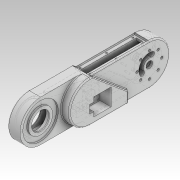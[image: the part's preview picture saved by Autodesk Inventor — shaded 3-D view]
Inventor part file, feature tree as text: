
AUTODESK INVENTOR PART (.ipt)
format: ipt  version: 2020 (Build 240168000, 168)  size: 708,096 bytes
history: native  units: mm
features: sketch x28, extrude x26, fillet x3, plane x2, revolve x2, projected_geometry x1
ambient origin geometry x8: Origin, YZ Plane, XZ Plane, XY Plane, X Axis, Y Axis, Z Axis, Center Point
bodies: Solid1 (feature_tree)
feature tree (62):
  extrude  "Extrusion1"  Depth=250.0mm
  extrude  "Extrusion3"  Depth=50.0mm TaperAngle=0.0deg
  extrude  "Extrusion6"  TaperAngle=0.0deg  [1 undecoded]
  extrude  "Extrusion7"  Depth=50.0mm
  extrude  "Extrusion8"  Depth=10.0mm TaperAngle=0.0deg
  extrude  "Extrusion9"  TaperAngle=0.0deg  [1 undecoded]
  extrude  "Extrusion10"  TaperAngle=30.0deg  [1 undecoded]
  extrude  "Extrusion11"  Depth=16.15mm
  extrude  "Extrusion12"  Depth=60.0mm
  plane  "Work Plane1"
  extrude  "Extrusion13"  Depth=10.0mm TaperAngle=0.0deg
  revolve  "Revolution1"  [1 undecoded]
  extrude  "Extrusion14"  Depth=86.0mm
  extrude  "Extrusion15"  Depth=4.0mm TaperAngle=0.0deg
  extrude  "Extrusion16"  Depth=70.0mm
  revolve  "Revolution2"  [1 undecoded]
  extrude  "Extrusion17"  Depth=7.3mm
  fillet  "Fillet1"  [1 undecoded]
  plane  "Work Plane2"
  extrude  "Extrusion18"  Depth=34.0mm
  extrude  "Extrusion19"  Depth=3.0mm TaperAngle=0.0deg
  extrude  "Extrusion20"  Depth=15.0mm TaperAngle=0.0deg
  extrude  "Extrusion21"  Depth=130.0mm
  extrude  "Extrusion25"  Depth=6.0mm TaperAngle=360.0deg
  extrude  "Extrusion22"  Depth=1.0mm
  fillet  "Fillet2"  Radius=5.2mm
  fillet  "Fillet3"  Radius=1.0mm
  extrude  "Extrusion23"  TaperAngle=90.0deg  [1 undecoded]
  extrude  "Extrusion24"  Depth=20.0mm
  extrude  "Extrusion26"  Depth=19.198622mm
  extrude  "Extrusion27"  Depth=50.0mm
  extrude  "Extrusion28"  TaperAngle=0.0deg  [1 undecoded]
  extrude  "CHOP"  Depth=12.0mm
  sketch  "Sketch1"  dims[d0=50.0mm d1=250.0mm]
  sketch  "Sketch3"  dims[d2=47.2mm d3=50.0mm d4=0.0mm]
  sketch  "Sketch6"  dims[d10=5.0mm d11=0.0mm d12=0.0mm]
  sketch  "Sketch7"  dims[d19=50.0mm d20=0.0mm d21=8.726646mm]
  projected_geometry  "Projected Loop1"
  sketch  "Sketch8"  dims[d22=75.0mm d25=10.0mm d26=0.0mm]
  sketch  "Sketch9"  dims[d27=50.0mm d30=0.0mm d31=0.0mm]
  sketch  "Sketch10"  dims[d33=30.0deg d34=30.0deg]
  sketch  "Sketch11"  dims[d35=0.0mm d36=0.0mm d37=16.15mm]
  sketch  "Sketch12"  dims[d38=3.3mm d39=60.0mm]
  sketch  "Sketch13"  dims[d40=80.0mm d42=360.0deg d44=10.0mm d45=0.0mm]
  sketch  "Sketch14"  dims[d50=42.0mm d51=42.0mm d52=0.0mm d53=0.0mm]
  sketch  "Sketch15"  dims[d54=38.0mm d55=86.0mm]
  sketch  "Sketch16"  dims[d56=59.0mm d57=4.0mm d58=0.0mm]
  sketch  "Sketch17"  dims[d59=-2.0mm d60=70.0mm]
  sketch  "Sketch18"  dims[d61=40.0mm d62=18.0mm d63=0.0mm]
  sketch  "Sketch19"  dims[d64=1.5mm d65=7.3mm d66=90.0deg]
  sketch  "Sketch20"  dims[d67=22.0mm d68=34.0mm]
  sketch  "Sketch21"  dims[d69=3.5mm d70=3.0mm d71=0.0mm]
  sketch  "Sketch22"  dims[d72=0.0mm d73=15.0mm d74=0.0mm]
  sketch  "Sketch23"  dims[d75=15.0mm d76=130.0mm]
  sketch  "Sketch24"  dims[d77=6.0mm d78=80.0mm d80=360.0deg]
  sketch  "Sketch25"  dims[d82=15.0mm d83=0.0mm d84=5.2mm d85=5.2mm d86=1.0mm]
  sketch  "Sketch26"  dims[d87=1.5mm d88=90.0deg]
  sketch  "Sketch27"  dims[d89=5.5mm d90=20.0mm]
  sketch  "Sketch28"  dims[d91=30.0deg d92=19.198622mm]
  sketch  "Sketch29"  dims[d93=15.0mm d94=0.0mm d95=50.0mm]
  sketch  "Sketch30"  dims[d96=30.0mm d97=0.0mm]
  sketch  "Sketch31"  dims[d98=8.0mm d99=12.0mm d100=6.1mm d101=13.0mm d102=125.0mm d103=75.0mm d104=0.0mm d105=0.0mm d106=2.1mm d107=10.0mm d108=10.0mm d109=32.0mm d110=110.0mm d111=0.0mm d112=3.0mm d113=3.0mm d114=5.0mm d115=1.0mm d116=4.0mm d117=0.0mm d118=4.0mm d119=4.0mm d120=32.25mm d121=0.0mm d122=3.0mm d124=0.5mm d125=0.0mm d126=3.0mm d127=2.0mm d128=8.0mm d129=8.0mm d130=4.0mm d131=4.0mm d132=3.9mm d133=6.0mm d134=0.0mm d135=4.0mm d136=0.0mm d137=60.0mm d138=0.5mm d139=0.0mm d140=3.0mm d141=10.0mm d142=20.0mm d143=15.0mm d144=0.0mm d145=8.0mm d146=23.75mm d147=0.0mm d148=15.0mm d149=23.75mm d150=0.0mm d151=200.998mm d152=0.0mm d123=0.872665mm]
note: 8 required parameter values undecoded (feature->parameter linkage not recoverable at this tier; creation-order binding heuristic only, values carry confidence <= 0.55)